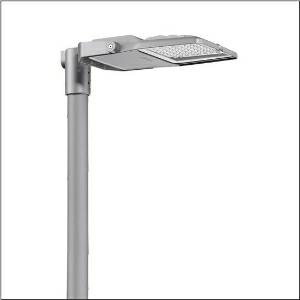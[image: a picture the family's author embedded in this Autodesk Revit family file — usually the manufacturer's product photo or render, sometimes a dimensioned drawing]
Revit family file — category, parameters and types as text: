
# Revit family: floodlight_fl_21_iq_mini___pl33t_5xa7771b2f3a_2789
name_source: partatom
category: Lighting Fixtures
units: mm (PartAtom-declared; Revit-internal decimal feet)

## family parameters
Cut with Voids When Loaded = No
Host = Face
Light Source = No
Part Type = Normal
Room Calculation Point = No
Round Connector Dimension = Use Diameter
Shared = No

## types (1)
- --- (1 x LED, 6170 lm, 45.5 W, 3000K)
    Apparent Load = 46 VA
    CIE Flux Codes = 26 75 99 100 100
    Color Rendering = 70
    Color Temperature = 3000K
    Default Elevation = 1800 mm
    Description = Floodlight FL 21 iQ mini, floodlight, primary light control with lens, of PMMA, primary optical cover: protective disc, of toughened safety glass, transparent, light distribution: PL33T, light emission: direct distribution, installation type: surface-mounted, lamps: LED, High Power LED, rated values: 6.170lm | 45,5W | 135,6lm/W (begin service life); end service life: 6.170lm | 48W; at 50% lumin. flux: 3.085lm | 21,5W | 143,5lm/W, colour temperature: 3000K, colour rendering: CRI > 70, light colour: 730, light setting 1 begin service life: 100% | 6.170lm | 45,5W | 135,6lm/W | 3.000K, light setting 1 end service life: 48W, further light settings possible, control: Auto-Match, Temp-Guard, Lumen-Switch, Night-Set, Smart-Wire, Light-Fading, Desk-Remote (wireless, voltage-free reading and setting of iQ features in the workshop via application-optimized NFC function/RFID function), optimised constant luminous flux control (CLO 2.0), pre-setting: linear dimming characteristic, with terminal, 6-pole, mains connection: 220..240V, AC, 50/60Hz, luminaire housing, of diecast aluminium, powder-coated, SITECO metallic grey (DB 702S), corrosivity category C5 mid according to DIN EN ISO 12944suitable for swimming poolschlorine-resistant, sealing non-destructively replaceable, please order mast flange separately, mast bracket, of steel, galvanised, powder-coated, SITECO metallic grey (DB 702S), protection rating (complete): IP66, insulation class (complete): insulation class II (safety insulation), certification: CE, ENEC, VDE, protection symbol: D, impact resistance: IK08, permissible operating ambient temperature: -40..+40°C, permissible operating ambient temperature for outdoor applications: -40..+50°C, standard: DIN EN 12944, LABS conformity tested according to VDMA 24364:2018-05, packaging unit: 1 piece

Light Distribution: PL33T
    Height = 70 mm
    Lamp = 1 x LED
    Lamp Light Flux = 6170 lm
    Lamp Power = 45.5 W
    Lamp count = 1
    Length = 485 mm
    Luminous efficacy = 136 lm/W
    Manufacturer = Siteco
    ModVariant = No
    Model = 5XA7771B2F3A
    Number of Poles = 1
    OnlyDefault = Yes
    Power Factor = 1
    Product Name = Floodlight FL 21 iQ mini | PL33T
    Product group = floodlight | pylon annexe
    ProductGroupID = 6201
    Protection Class = Protection class II
    Protection Degree = IP 66
    RLX_Detail_Level = 1
    RLX_Emergency_Light_Flux = 0 lm
    RLX_Emergency_Type = 0
    RLX_Emergency_Type_DB = No
    RlxData = <blob elided: 101361 chars, md5=f03384c3>
    Socket = socket
    Standby Power = 0 W
    System Light Flux = 6170 lm
    System Power = 46 W
    Type Comments = factory setting: luminous flux: 100 % | dim-lin: 254 | 463 mA
    Type Image = l_1007125.jpg
    URL = http://relux.com
    VarID = @adj_149779
    Voltage = 0 V
    Weight = 0.00 kg
    Width = 337 mm

## geometry (parser evidence)
native form markers: Blend x4, Sweep x11
no freeform markers — native parametric forms only
